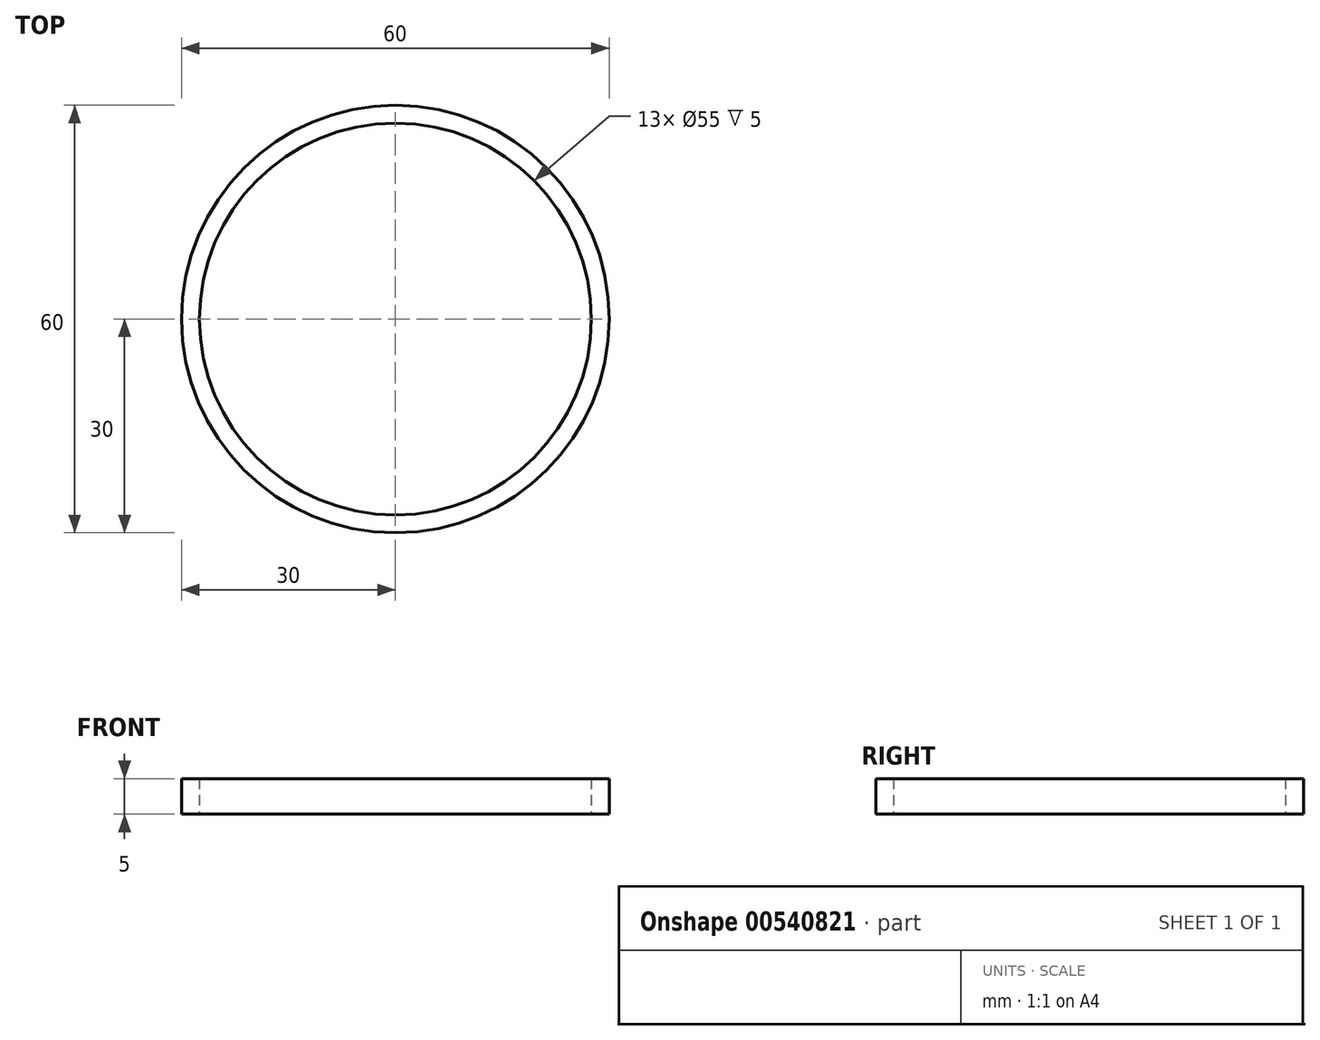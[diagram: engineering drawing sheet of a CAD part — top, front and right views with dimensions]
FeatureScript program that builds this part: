
annotation { "Feature Type Name" : "Feature", "Feature Type Description" : "" }
export const myFeature = defineFeature(function(context is Context, id is Id, definition is map)
    precondition{}
    {
        {
            var Q0;
            Q0=qCreatedBy(makeId("Top.planeOp"),FACE);
            var sketch = newSketch(context, id + "F0", { "sketchPlane" : qUnion([Q0])});
            skCircle(sketch, "E0", {"center": v(0, 0) * mm, "radius": 27.5 * mm});
            skCircle(sketch, "E1", {"center": v(0, 0) * mm, "radius": 30 * mm});
            skSolve(sketch);
        }
        {
            var Q0;
            Q0=qCreatedBy(makeId("Top.planeOp"),FACE);
            var sketch = newSketch(context, id + "F1", { "sketchPlane" : qUnion([Q0])});
            skCircle(sketch, "E2", {"center": v(0, 0) * mm, "radius": 30 * mm});
            skSolve(sketch);
        }
        {
            var Q0;
            Q0 = qSketchRegion(id + "F0", true);
            var Q1;
            Q1 = qSketchRegion(id + "F1", true);
            extrude(context, id + "F2", {"entities" : qUnion([Q0, Q1]), "depth" : 5 * mm, "offsetDistance" : 25 * mm});
        }
    });
